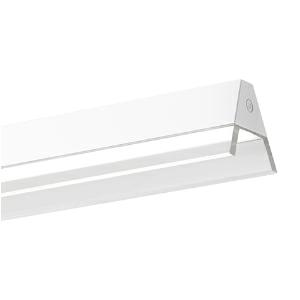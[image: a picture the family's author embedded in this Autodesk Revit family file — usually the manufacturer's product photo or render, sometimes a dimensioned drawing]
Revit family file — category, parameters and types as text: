
# Revit family: 3f_filippi_-_3f_mirella_di_sp_3f_filippi_-_10927_-_3f_mirella_wh_di_60_14_dali_sp_l2200_ca54
name_source: partatom
category: Lighting Fixtures
units: mm (PartAtom-declared; Revit-internal decimal feet)

## family parameters
Cut with Voids When Loaded = No
Host = Face
Light Source = No
Part Type = Normal
Room Calculation Point = No
Round Connector Dimension = Use Diameter
Shared = No

## types (1)
- 3F Filippi - 3F Mirella DI SP (1 x LED, 8907 lm, 84 W, 4000 K)
    Apparent Load = 84 VA
    Approval mark = ENEC
    CIE Flux Codes = 62 95 99 77 100
    Color Rendering = 80
    Color Temperature = 4000 K
    Control Gear = Electronic transformer
    Default Elevation = 1800 mm
    Description = ILLUMINOTECHNICAL
Luminous efficiency 100% (DLOR 77%, ULOR 23%).
Initial luminous flux of the luminaire 8907 lm.
Symmetric direct-indirect distribution.
Installation Interdistance Transv.D = 1.65 x hu - Long.D = 1.26 x hu.
Average luminance <3000 cd/m² for radial angles >65°.
Tabular UGR (CIE 117 - 4H-8H; S=0.25H; 70/50/20): RUG 16.2 - 17.3.
Beam angle: 89° - 96°.
Luminous efficacy 106 lm/W.
Lifetime (L93/B10): 30000 h. (tq+25°C)
Lifetime (L90/B10): 50000 h. (tq+25°C)
Lifetime (L85/B10): 80000 h. (tq+25°C)
Lifetime (L80/B10): 100000 h. (tq+25°C)
Sudden decreased luminous flux after 50000 hours: 0% (C0).
Photobiological safety in compliance with IEC/TR 62778: RG0 risk exempt, (IEC 62471).
In compliance with IEC/EN 62722-2-1 - IEC/EN 62717 standards.

SOURCE
One 60W/840 linear LED module for direct lighting + one 14W/840 linear LED module for indirect lighting.
Energy efficiency class (UE 2019/2020 - UE 2019/2015): D, E.
CIE 13.3 Colour rendering index: CRI >80 (R9 <50%).
IES TM-30 Fidelity Index: Rf = 84 Rg = 95.
CCT nominal colour temperature 4000 K.
Colour initial tolerance (MacAdam): SDCM 3.

MECHANICAL
Housing in white painted extruded aluminium.
Methacrylate (PMMA) primary lens for total source shielding.
Highly aesthetic external lens in transparent methacrylate (PMMA) for optimizing light distribution.
Flat transparent prismatic methacrylate (PMMA) filter, multi-lenticular exterior, anti-glare.
Upper film in translucent polycarbonate, self-extinguishing, UV stabilised.
White painted aluminium end caps.
Luminaire with limited surface temperature. - D - (EN 60598-2-24)
Dimensions: 2200x112 mm, height 91 mm. Weight 8.805 kg.
IP40 protection degree.
Mechanical strength to impacts IK06 (1 joule).
Glow-wire test resistance 650°C.

ELECTRICAL
Halogen Free DALI-2, PUSH-DIM, electronic wiring 230V-50/60Hz, power factor 0.95 at full load, THD <25%, constant output current, SELV, class I, 2 driver, 2 DALI addresses.
Power of the luminaire 84 W.
CE - IEC 60598-1 - EN 60598-1.
SAFE FLICKER: PstLM=<1 and SVM=<0.4 (IEC TR 61547-1 and IEC TR 63158), to ensure a more comfortable and safe light.
Luminaire compliant with EN 60598-2-22 for power supply from a centralised emergency system CPSS (Central Power Supply System), not incorporated in the luminaire - high risk areas excluded. The default power and flux are 100% in AC and 15% in DC.
Ambient temperature from 0°C to +25°C.
Temperature class T6 max 85°C.
Relative humidity UR: <85%.

INSTALLATION
Suspended.

SUPPLIED
Suspensions with chrome bosses and quick adjusters, 2 m galvanised steel cable.
Transparent 2.3 m 5x0.75 mm² power cable with white power supply case for mounting on the ceiling.

APPLICATIONS
Environments involving accurate visual tasks where a diffused and soft light for an optimum visual comfort and the source total shielding are required.
In environments with VDTs, managerial offices and staterooms.

LIGHT MANAGEMENT
Recommended minimum setting: 10%.
The device, equipped with DALI-2 driver, can be controlled manually with 3F Easy Dim technology or automatically/manually with 3F Smart Dimming technology and/or centralised DALI systems.
DALI-2 certification guarantees interoperability with other devices with the same certification.
In electrical systems without a regulation system (manual or automatic) and DALI bus, a suitable jumper must be made on the DA-DA terminals of the appliance.

WARNING
Luminaire designed for disposal/recycling at end-of-life.
Replaceable (LED only) light source by a professional. Replaceable control gear by a professional.
    Height = 91 mm
    Lamp = 1 x LED
    Lamp Light Flux = 8907 lm
    Lamp Power = 84 W
    Lamp count = 1
    Length = 2200 mm
    Lifetime = 50000 h
    Luminous efficacy = 106 lm/W
    Manufacturer = 3F Filippi
    ModVariant = No
    Model = 3F Filippi - 10927 - 3F Mirella WH DI 60+14 DALI SP L2200
    Mounting Place = Ceiling
    Mounting Type = Pendant
    Number of Poles = 1
    OnlyDefault = Yes
    Power Factor = 1
    Product Name = 3F Filippi - 3F Mirella DI SP
    Product group = pendant luminaire
    ProductGroupID = 9
    Protection Class = Protection class I
    Protection Degree = IP 40
    RLX_Detail_Level = 1
    RLX_Emergency_Light_Flux = 0 lm
    RLX_Emergency_Type = 0
    RLX_Emergency_Type_DB = No
    RlxData = <blob elided: 66193 chars, md5=1ec98150>
    Socket = socket
    Standby Power = 0 W
    System Light Flux = 8907 lm
    System Power = 84 W
    Type Comments = Product without accessories
    Type Image = 3ffilippi_3f_mirella_wh.jpg
    URL = http://relux.com
    VarID = ---
    Voltage = 0 V
    Weight = 0.00 kg
    Width = 112 mm

## geometry (parser evidence)
native form markers: Blend x4, Sweep x13
no freeform markers — native parametric forms only
